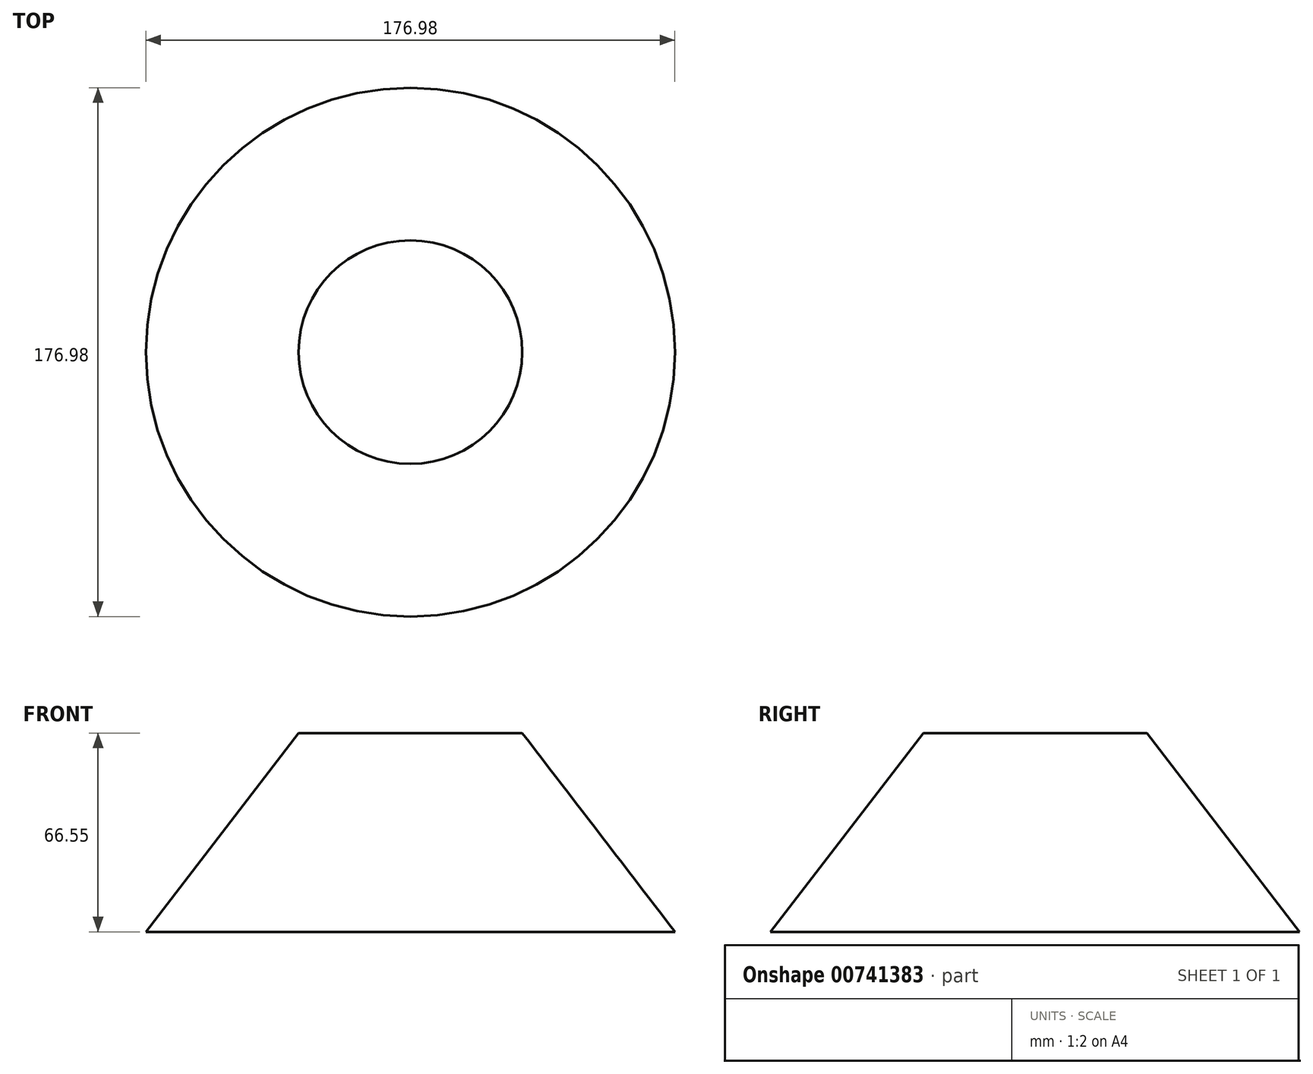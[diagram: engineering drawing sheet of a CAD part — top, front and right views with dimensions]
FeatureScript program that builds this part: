
annotation { "Feature Type Name" : "Feature", "Feature Type Description" : "" }
export const myFeature = defineFeature(function(context is Context, id is Id, definition is map)
    precondition{}
    {
        {
            var Q0;
            Q0=qCreatedBy(makeId("Front.planeOp"),FACE);
            var sketch = newSketch(context, id + "F0", { "sketchPlane" : qUnion([Q0])});
            skLineSegment(sketch, "E0", {"start": v(-57.06, 33.83) * mm, "end": v(-57.06, -32.72) * mm});
            skLineSegment(sketch, "E1", {"start": v(-57.06, -32.72) * mm, "end": v(31.43, -32.72) * mm});
            skLineSegment(sketch, "E2", {"start": v(31.43, -32.72) * mm, "end": v(-19.63, 33.83) * mm});
            skLineSegment(sketch, "E3", {"start": v(-19.63, 33.83) * mm, "end": v(-57.06, 33.83) * mm});
            skSolve(sketch);
        }
        {
            var Q0;
            Q0=makeQuery(id+"F0.imprint","IMPRINT",FACE,{"disambiguationData":[TD([[makeQuery(id+"F0.imprint","IMPRINT",EDGE,{"derivedFrom":sQuery(id+"F0.wireOp",EDGE,"E0")}),1.0]])]});
            var Q1;
            Q1=sQuery(id+"F0.wireOp",EDGE,"E0");
            revolve(context, id + "F1", {"surfaceOperationType" : NewSurfaceOperationType.NEW, "entities" : qUnion([Q0]), "axis" : qUnion([Q1]), "revolveType" : RevolveType.FULL});
        }
    });
